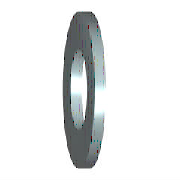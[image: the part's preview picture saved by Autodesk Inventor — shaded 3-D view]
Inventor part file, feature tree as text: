
AUTODESK INVENTOR PART (.ipt)
format: ipt  version: 2013 (Build 170138000, 138)  size: 107,008 bytes
history: native  units: mm (DEFAULTED — no unit token found)
features: other x1, plane x1, sketch x1
ambient origin geometry x7: Origin, YZ Plane, XY Plane, X Axis, Y Axis, Z Axis, Center Point
bodies: Solid1 (feature_tree), Body (feature_tree)
feature tree (3):
  other  "Work Axis1"
  plane  "Work Plane1"
  sketch  "Sketch"  dims[d0=7.1374mm d1=15.875mm d2=1.651mm d3=0.0mm d4=0.0mm d5=0.0mm d6=0.0mm d7=0.0mm]
